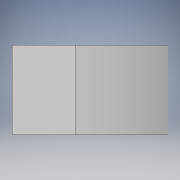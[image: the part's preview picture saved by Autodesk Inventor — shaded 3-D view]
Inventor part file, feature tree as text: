
AUTODESK INVENTOR PART (.ipt)
format: ipt  version: 2018.2 (Build 222227000, 227)  size: 93,696 bytes
history: native  units: mm
features: other x1, extrude x1, sketch x1
ambient origin geometry x8: Origin, YZ Plane, XZ Plane, XY Plane, X Axis, Y Axis, Z Axis, Center Point
bodies: Body1 (feature_tree)
feature tree (3):
  other  "ソリッド1"
  extrude  "押し出し1"  Depth=3000.0mm
  sketch  "スケッチ1"
